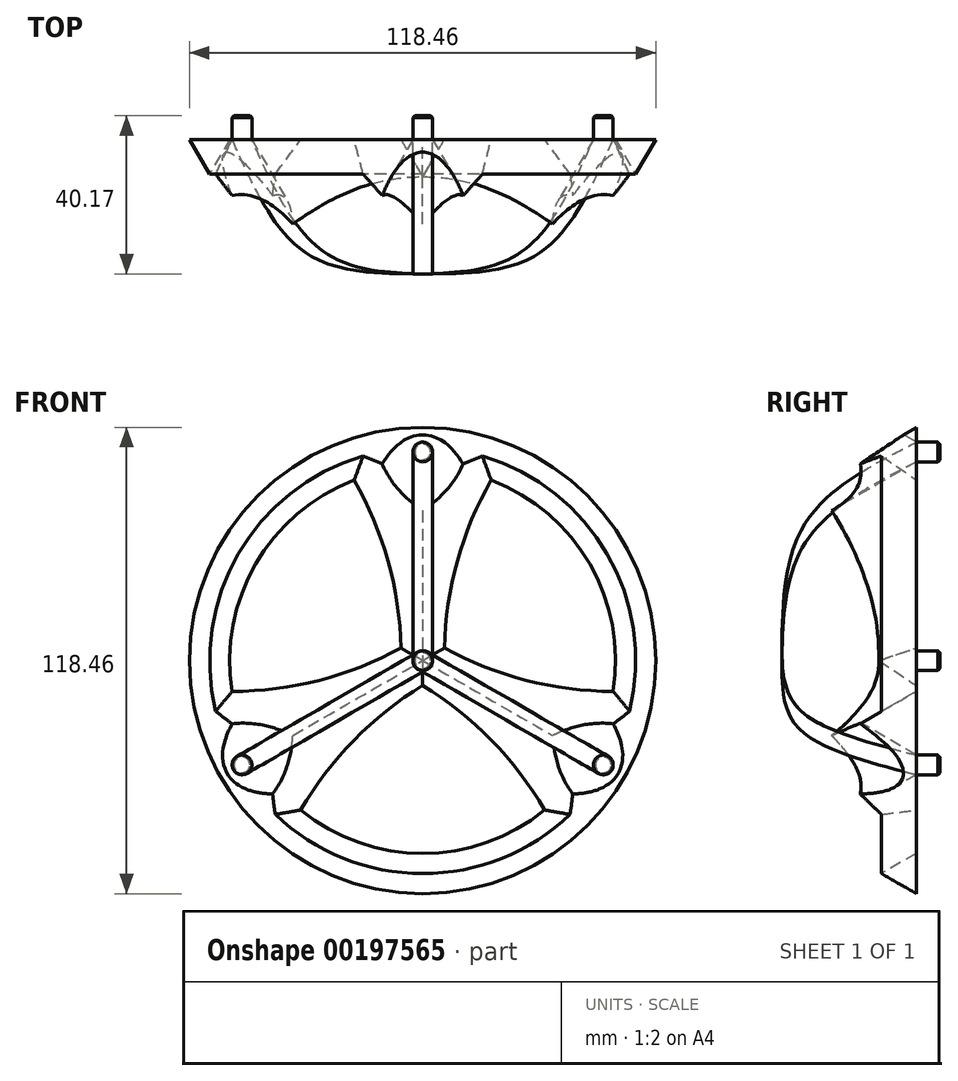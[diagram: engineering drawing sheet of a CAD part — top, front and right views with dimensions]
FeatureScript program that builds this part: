
annotation { "Feature Type Name" : "Feature", "Feature Type Description" : "" }
export const myFeature = defineFeature(function(context is Context, id is Id, definition is map)
    precondition{}
    {
        {
            var Q0;
            Q0=qCreatedBy(makeId("Front.planeOp"),FACE);
            var sketch = newSketch(context, id + "F0", { "sketchPlane" : qUnion([Q0])});
            skCircle(sketch, "E0.0", {"center": v(0, 0) * mm, "radius": 59.23 * mm});
            skArc(sketch, "E1.0", {"start": v(-30.98, -37.98) * mm, "mid": v(0, -49.01) * mm, "end": v(30.98, -37.98) * mm});
            skArc(sketch, "E2.0", {"start": v(-5.73, 7.66) * mm, "mid": v(-9.43, 27.4) * mm, "end": v(-17.4, 45.82) * mm});
            skArc(sketch, "E3", {"start": v(-3.77, -8.8) * mm, "mid": v(0, -9.56) * mm, "end": v(3.77, -8.8) * mm});
            skArc(sketch, "E4.MirrorCS", {"start": v(5.73, 7.66) * mm, "mid": v(9.43, 27.4) * mm, "end": v(17.4, 45.82) * mm});
            skArc(sketch, "E5.1.0", {"start": v(-3.77, -8.8) * mm, "mid": v(-19, -21.86) * mm, "end": v(-30.98, -37.98) * mm});
            skArc(sketch, "E5.1.1", {"start": v(-9.5, 1.13) * mm, "mid": v(-28.44, -5.53) * mm, "end": v(-48.38, -7.84) * mm});
            skArc(sketch, "E5.2.0", {"start": v(9.5, 1.13) * mm, "mid": v(28.44, -5.53) * mm, "end": v(48.38, -7.84) * mm});
            skArc(sketch, "E5.2.1", {"start": v(3.77, -8.8) * mm, "mid": v(19, -21.86) * mm, "end": v(30.98, -37.98) * mm});
            skArc(sketch, "E6.trimOffspring", {"start": v(9.5, 1.13) * mm, "mid": v(8.28, 4.78) * mm, "end": v(5.73, 7.66) * mm});
            skArc(sketch, "E7.trimOffspring", {"start": v(-5.73, 7.66) * mm, "mid": v(-8.28, 4.78) * mm, "end": v(-9.5, 1.13) * mm});
            skArc(sketch, "E8.trimOffspring", {"start": v(48.38, -7.84) * mm, "mid": v(42.45, 24.5) * mm, "end": v(17.4, 45.82) * mm});
            skArc(sketch, "E9.trimOffspring", {"start": v(-17.4, 45.82) * mm, "mid": v(-42.45, 24.5) * mm, "end": v(-48.38, -7.84) * mm});
            skCircle(sketch, "E10", {"center": v(0, 53) * mm, "radius": 2.5 * mm});
            skCircle(sketch, "E11.1.0", {"center": v(-45.9, -26.5) * mm, "radius": 2.5 * mm});
            skCircle(sketch, "E11.2.0", {"center": v(45.9, -26.5) * mm, "radius": 2.5 * mm});
            skSolve(sketch);
        }
        {
            var Q0;
            Q0=makeQuery(id+"F0.imprint","IMPRINT",FACE,{"disambiguationData":[TD([[makeQuery(id+"F0.imprint","IMPRINT",EDGE,{"derivedFrom":sQuery(id+"F0.wireOp",EDGE,"E0.0")}),1.0]])]});
            extrude(context, id + "F1", {"entities" : qUnion([Q0]), "depth" : 25 * mm, "hasDraft" : true, "draftAngle" : 30 * degree, "draftPullDirection" : true});
        }
        {
            var Q0;
            Q0=makeQuery(id+"F1.opExtrude","CAP_FACE",FACE,{"disambiguationData":[OSD([sQuery(id+"F0.wireOp",EDGE,"E0.0"),sQuery(id+"F0.wireOp",EDGE,"E1.0"),sQuery(id+"F0.wireOp",EDGE,"E2.0"),sQuery(id+"F0.wireOp",EDGE,"E3"),sQuery(id+"F0.wireOp",EDGE,"E4.MirrorCS"),sQuery(id+"F0.wireOp",EDGE,"E5.1.0"),sQuery(id+"F0.wireOp",EDGE,"E5.1.1"),sQuery(id+"F0.wireOp",EDGE,"E5.2.0"),sQuery(id+"F0.wireOp",EDGE,"E5.2.1"),sQuery(id+"F0.wireOp",EDGE,"E6.trimOffspring"),sQuery(id+"F0.wireOp",EDGE,"E7.trimOffspring"),sQuery(id+"F0.wireOp",EDGE,"E8.trimOffspring"),sQuery(id+"F0.wireOp",EDGE,"E9.trimOffspring"),sQuery(id+"F0.wireOp",EDGE,"E10"),sQuery(id+"F0.wireOp",EDGE,"E11.1.0"),sQuery(id+"F0.wireOp",EDGE,"E11.2.0")])],"isStart":true});
            var sketch = newSketch(context, id + "F2", { "sketchPlane" : qUnion([Q0])});
            skCircle(sketch, "E12", {"center": v(0, 0) * mm, "radius": 2.5 * mm});
            skSolve(sketch);
        }
        {
            var Q0;
            Q0=makeQuery(id+"F2.imprint","IMPRINT",FACE,{"disambiguationData":[TD([[makeQuery(id+"F2.imprint","IMPRINT",EDGE,{"derivedFrom":sQuery(id+"F2.wireOp",EDGE,"E12")}),1.0]])]});
            extrude(context, id + "F3", {"entities" : qUnion([Q0]), "operationType" : NewBodyOperationType.ADD, "depth" : 6 * mm});
        }
        {
            var Q0;
            Q0=makeQuery(id+"F3.opExtrude","CAP_FACE",FACE,{"disambiguationData":[OSD([sQuery(id+"F2.wireOp",EDGE,"E12")])],"isStart":false});
            chamfer(context, id + "F4", {"entities" : qUnion([Q0]), "width" : .5 * mm, "tangentPropagation" : true});
        }
        {
            var Q0;
            Q0=makeQuery(id+"F1.opExtrude","CAP_FACE",FACE,{"disambiguationData":[OSD([sQuery(id+"F0.wireOp",EDGE,"E0.0"),sQuery(id+"F0.wireOp",EDGE,"E1.0"),sQuery(id+"F0.wireOp",EDGE,"E2.0"),sQuery(id+"F0.wireOp",EDGE,"E3"),sQuery(id+"F0.wireOp",EDGE,"E4.MirrorCS"),sQuery(id+"F0.wireOp",EDGE,"E5.1.0"),sQuery(id+"F0.wireOp",EDGE,"E5.1.1"),sQuery(id+"F0.wireOp",EDGE,"E5.2.0"),sQuery(id+"F0.wireOp",EDGE,"E5.2.1"),sQuery(id+"F0.wireOp",EDGE,"E6.trimOffspring"),sQuery(id+"F0.wireOp",EDGE,"E7.trimOffspring"),sQuery(id+"F0.wireOp",EDGE,"E8.trimOffspring"),sQuery(id+"F0.wireOp",EDGE,"E9.trimOffspring"),sQuery(id+"F0.wireOp",EDGE,"E10"),sQuery(id+"F0.wireOp",EDGE,"E11.1.0"),sQuery(id+"F0.wireOp",EDGE,"E11.2.0")])],"isStart":true});
            var sketch = newSketch(context, id + "F5", { "sketchPlane" : qUnion([Q0])});
            skCircle(sketch, "E13", {"center": v(0, 53) * mm, "radius": 2.5 * mm});
            skCircle(sketch, "E14", {"center": v(-45.9, -26.5) * mm, "radius": 2.5 * mm});
            skCircle(sketch, "E15", {"center": v(45.9, -26.5) * mm, "radius": 2.5 * mm});
            skSolve(sketch);
        }
        {
            var Q0;
            Q0=makeQuery(id+"F5.imprint","IMPRINT",FACE,{"disambiguationData":[TD([[makeQuery(id+"F5.imprint","IMPRINT",EDGE,{"derivedFrom":sQuery(id+"F5.wireOp",EDGE,"E13")}),-1.0]])]});
            var Q1;
            Q1=makeQuery(id+"F5.imprint","IMPRINT",FACE,{"disambiguationData":[TD([[makeQuery(id+"F5.imprint","IMPRINT",EDGE,{"derivedFrom":sQuery(id+"F5.wireOp",EDGE,"E14")}),-1.0]])]});
            var Q2;
            Q2=makeQuery(id+"F5.imprint","IMPRINT",FACE,{"disambiguationData":[TD([[makeQuery(id+"F5.imprint","IMPRINT",EDGE,{"derivedFrom":sQuery(id+"F5.wireOp",EDGE,"E15")}),-1.0]])]});
            extrude(context, id + "F6", {"entities" : qUnion([Q0, Q1, Q2]), "depth" : 6 * mm});
        }
        {
            var Q0;
            Q0=makeQuery(id+"F6.opExtrude","CAP_FACE",FACE,{"disambiguationData":[OSD([sQuery(id+"F5.wireOp",EDGE,"E14")])],"isStart":false});
            var Q1;
            Q1=makeQuery(id+"F6.opExtrude","CAP_FACE",FACE,{"disambiguationData":[OSD([sQuery(id+"F5.wireOp",EDGE,"E15")])],"isStart":false});
            var Q2;
            Q2=makeQuery(id+"F6.opExtrude","CAP_FACE",FACE,{"disambiguationData":[OSD([sQuery(id+"F5.wireOp",EDGE,"E13")])],"isStart":false});
            chamfer(context, id + "F7", {"entities" : qUnion([Q0, Q1, Q2]), "width" : .5 * mm, "tangentPropagation" : true});
        }
        {
            var Q0;
            Q0=makeQuery(id+"F6.opExtrude","CAP_FACE",FACE,{"disambiguationData":[OSD([sQuery(id+"F5.wireOp",EDGE,"E13")])],"isStart":true});
            var sketch = newSketch(context, id + "F8", { "sketchPlane" : qUnion([Q0])});
            skLineSegment(sketch, "E16", {"start": v(0, 53) * mm, "end": v(0, 0) * mm, "construction": true});
            skCircle(sketch, "E17", {"center": v(0, 53) * mm, "radius": 5.5 * mm});
            skCircle(sketch, "E18.1.0", {"center": v(-45.9, -26.5) * mm, "radius": 5.5 * mm});
            skCircle(sketch, "E18.2.0", {"center": v(45.9, -26.5) * mm, "radius": 5.5 * mm});
            skPoint(sketch, "E18.center", {"position": v(0, 0) * mm});
            skSolve(sketch);
        }
        {
            var Q0;
            Q0=qCreatedBy(makeId("Right.planeOp"),FACE);
            var sketch = newSketch(context, id + "F9", { "sketchPlane" : qUnion([Q0])});
            skFitSpline(sketch, "E19", {"points": [v(-34.17, 0) * mm, v(-28.36, 32.18) * mm, v(0, 53) * mm], "startDerivative": vector(1.06, 71.62) * mm, "endDerivative": vector(66.9, 34.3) * mm});
            skLineSegment(sketch, "E20", {"start": v(0, 0) * mm, "end": v(-34.17, 0) * mm});
            skSolve(sketch);
        }
        {
            var Q0;
            Q0=makeQuery(id+"F8.imprint","IMPRINT",FACE,{"disambiguationData":[TD([[makeQuery(id+"F8.imprint","IMPRINT",EDGE,{"derivedFrom":makeQuery(id+"F6.opExtrude","CAP_EDGE",EDGE,{"disambiguationData":[OSD([sQuery(id+"F5.wireOp",EDGE,"E13")])],"isStart":true})}),1.0]])]});
            var Q1;
            Q1=sQuery(id+"F9.wireOp",EDGE,"E19");
            sweep(context, id + "F10", {"profiles" : qUnion([Q0]), "path" : qUnion([Q1]), "keepProfileOrientation" : true});
        }
        {
            var Q0;
            Q0=makeQuery(id+"F10.opSweep","SWEPT_BODY",BODY,{"disambiguationData":[OSD([sQuery(id+"F5.wireOp",EDGE,"E13"),sQuery(id+"F9.wireOp",EDGE,"E19")])]});
            var Q1;
            Q1=sQuery(id+"F9.wireOp",EDGE,"E20");
            circularPattern(context, id + "F11", {"entities" : qUnion([Q0]), "axis" : qUnion([Q1]), "angle" : 360 * degree, "instanceCount" : 3, "equalSpace" : true});
        }
    });
